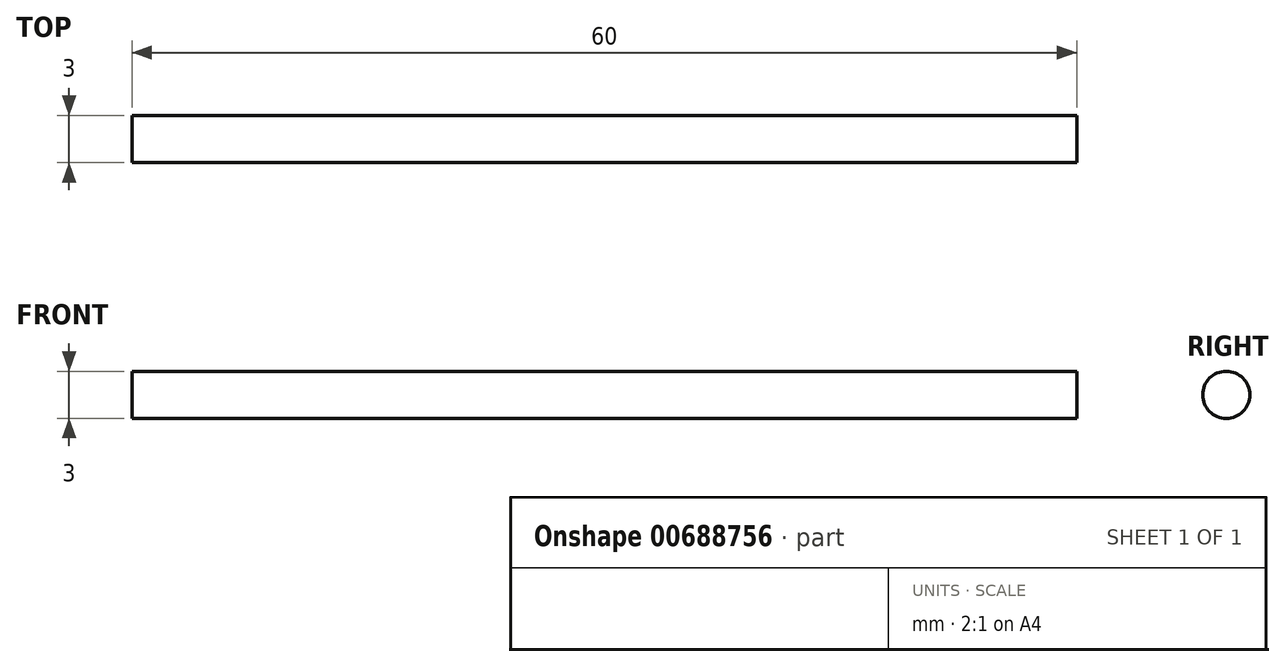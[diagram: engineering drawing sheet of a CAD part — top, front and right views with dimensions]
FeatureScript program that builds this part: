
annotation { "Feature Type Name" : "Feature", "Feature Type Description" : "" }
export const myFeature = defineFeature(function(context is Context, id is Id, definition is map)
    precondition{}
    {
        {
            var Q0;
            Q0=qCreatedBy(makeId("Right.planeOp"),FACE);
            var sketch = newSketch(context, id + "F0", { "sketchPlane" : qUnion([Q0])});
            skCircle(sketch, "E0", {"center": v(0, 0) * mm, "radius": 1.5 * mm});
            skSolve(sketch);
        }
        {
            var Q0;
            Q0=qSketchRegion(id+"F0",true);
            extrude(context, id + "F1", {"entities" : qUnion([Q0]), "depth" : 60 * mm, "offsetDistance" : 25 * mm, "symmetric" : true});
        }
    });
